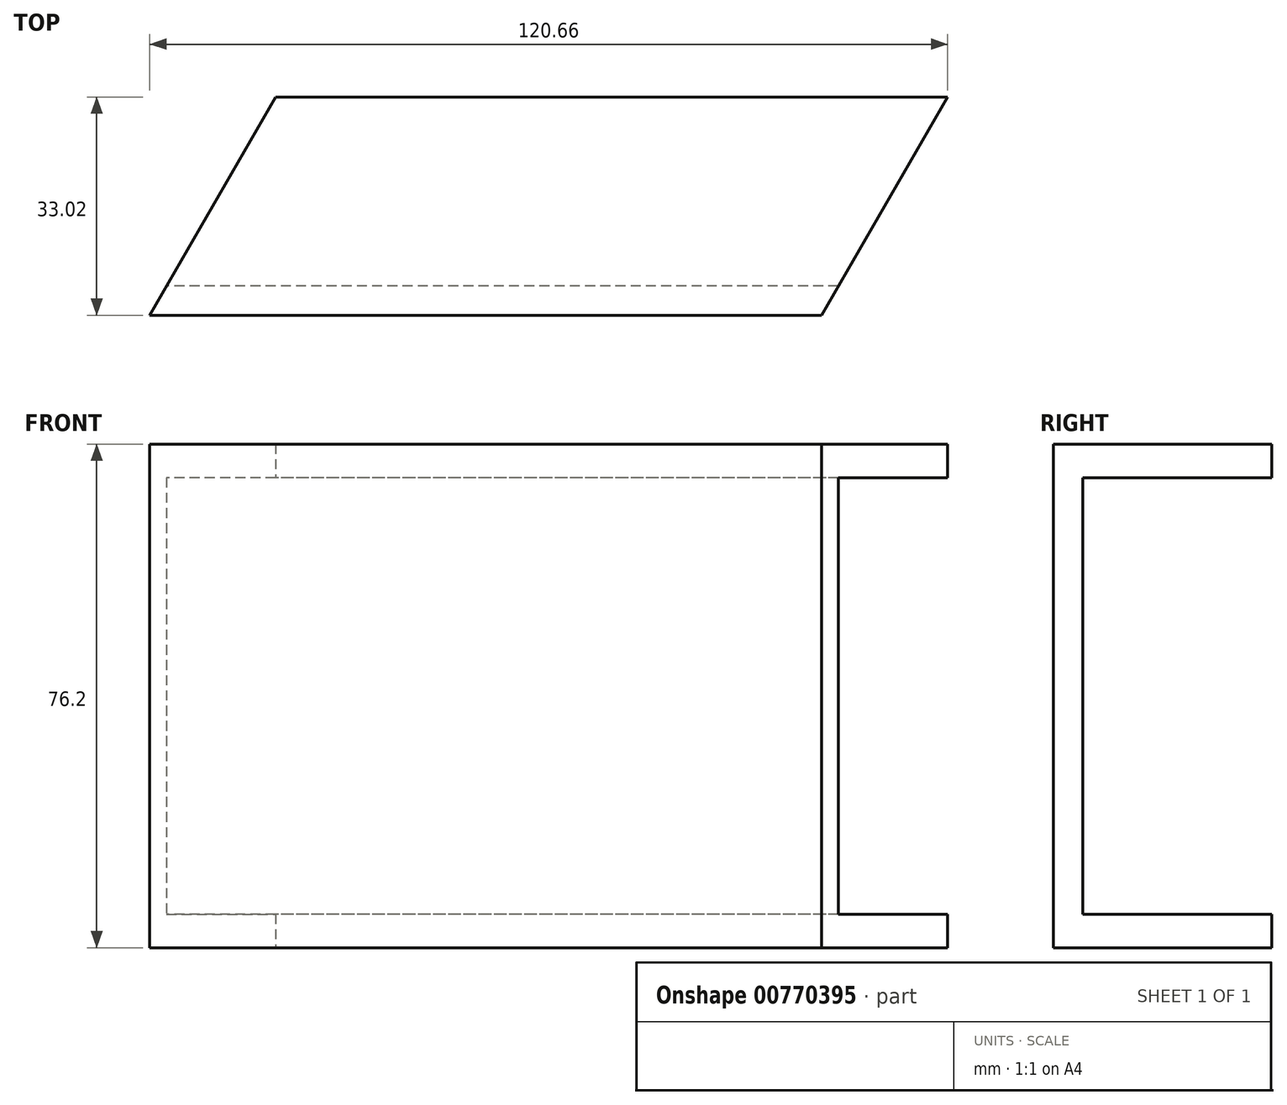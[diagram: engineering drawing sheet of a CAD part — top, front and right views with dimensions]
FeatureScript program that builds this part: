
annotation { "Feature Type Name" : "Feature", "Feature Type Description" : "" }
export const myFeature = defineFeature(function(context is Context, id is Id, definition is map)
    precondition{}
    {
        {
            var Q0;
            Q0=qCreatedBy(makeId("Top.planeOp"),FACE);
            var sketch = newSketch(context, id + "F0", { "sketchPlane" : qUnion([Q0])});
            skLineSegment(sketch, "E0", {"start": v(-55.08, -0.83) * mm, "end": v(46.52, -0.83) * mm});
            skLineSegment(sketch, "E1", {"start": v(46.52, -0.83) * mm, "end": v(27.46, -33.85) * mm});
            skLineSegment(sketch, "E2", {"start": v(27.46, -33.85) * mm, "end": v(-74.14, -33.85) * mm});
            skLineSegment(sketch, "E3", {"start": v(-74.14, -33.85) * mm, "end": v(-55.08, -0.83) * mm});
            skSolve(sketch);
        }
        {
            var Q0;
            Q0=makeQuery(id+"F0.imprint","IMPRINT",FACE,{"disambiguationData":[TD([[makeQuery(id+"F0.imprint","IMPRINT",EDGE,{"derivedFrom":sQuery(id+"F0.wireOp",EDGE,"E0")}),-1.0]])]});
            extrude(context, id + "F1", {"entities" : qUnion([Q0]), "depth" : 76.2 * mm, "offsetDistance" : 25.4 * mm});
        }
        {
            var Q0;
            Q0=makeQuery(id+"F1.opExtrude","SWEPT_FACE",FACE,{"disambiguationData":[OSD([sQuery(id+"F0.wireOp",EDGE,"E1")])]});
            var sketch = newSketch(context, id + "F2", { "sketchPlane" : qUnion([Q0])});
            skLineSegment(sketch, "E4", {"start": v(22.54, 71.12) * mm, "end": v(-10.51, 71.12) * mm});
            skLineSegment(sketch, "E5", {"start": v(-10.51, 71.12) * mm, "end": v(-10.51, 5.08) * mm});
            skLineSegment(sketch, "E6", {"start": v(-10.51, 5.08) * mm, "end": v(22.54, 5.08) * mm});
            skSolve(sketch);
        }
        {
            var Q0;
            Q0=makeQuery(id+"F1.opExtrude","SWEPT_FACE",FACE,{"disambiguationData":[OSD([sQuery(id+"F0.wireOp",EDGE,"E0")])]});
            var sketch = newSketch(context, id + "F3", { "sketchPlane" : qUnion([Q0])});
            skLineSegment(sketch, "E7", {"start": v(-46.52, 38.1) * mm, "end": v(55.08, 38.1) * mm});
            skSolve(sketch);
        }
        {
            var Q0;
            {var subQ0=sQuery(id+"F2.wireOp",EDGE,"E4");Q0=makeQuery(id+"F2.imprint","IMPRINT",FACE,{"disambiguationData":[TD([[makeQuery(id+"F2.imprint","IMPRINT",EDGE,{"derivedFrom":subQ0}),1.0]])]});}
            var Q1;
            Q1=sQuery(id+"F3.wireOp",EDGE,"E7");
            sweep(context, id + "F4", {"operationType" : NewBodyOperationType.REMOVE, "profiles" : qUnion([Q0]), "path" : qUnion([Q1])});
        }
    });
